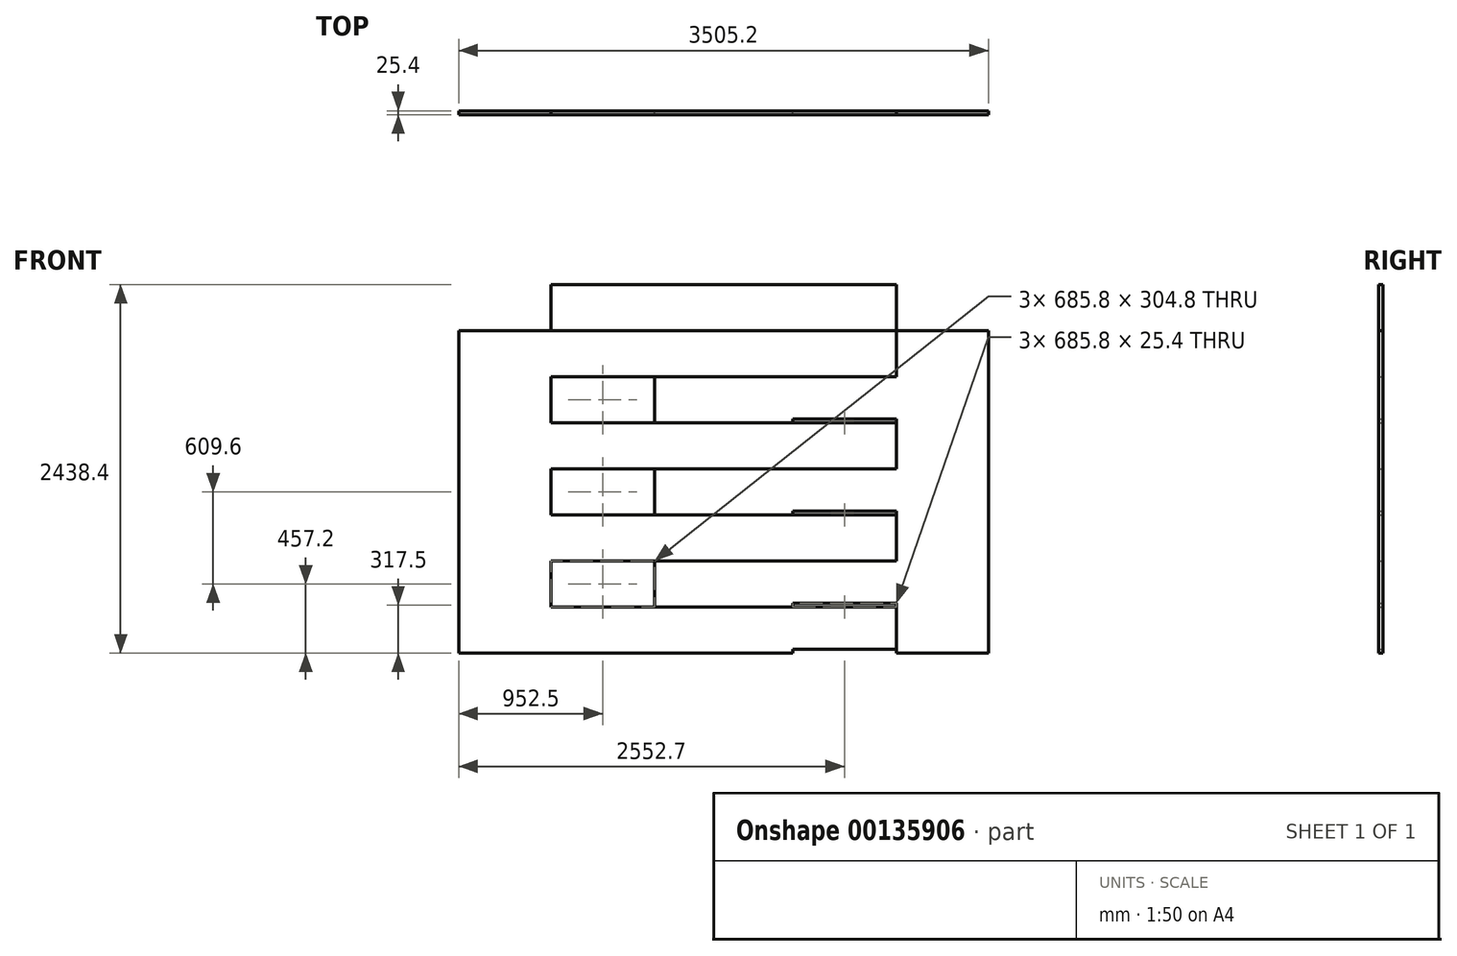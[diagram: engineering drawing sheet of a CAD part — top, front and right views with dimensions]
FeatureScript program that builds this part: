
annotation { "Feature Type Name" : "Feature", "Feature Type Description" : "" }
export const myFeature = defineFeature(function(context is Context, id is Id, definition is map)
    precondition{}
    {
        {
            var Q0;
            Q0=qCreatedBy(makeId("Front.planeOp"),FACE);
            var sketch = newSketch(context, id + "F0", { "sketchPlane" : qUnion([Q0])});
            skLineSegment(sketch, "E0.bottom", {"start": v(1143, 1270) * mm, "end": v(-1143, 1270) * mm});
            skLineSegment(sketch, "E0.top", {"start": v(1143, -1270) * mm, "end": v(-1143, -1270) * mm});
            skLineSegment(sketch, "E0.left", {"start": v(1143, 1270) * mm, "end": v(1143, 558.8) * mm});
            skLineSegment(sketch, "E0.right", {"start": v(-1143, 1270) * mm, "end": v(-1143, 863.6) * mm});
            skPoint(sketch, "E0.middle", {"position": v(0, 0) * mm});
            skLineSegment(sketch, "E1.bottom", {"start": v(-457.2, -1270) * mm, "end": v(457.2, -1270) * mm});
            skLineSegment(sketch, "E1.top", {"start": v(-457.2, 762) * mm, "end": v(457.2, 762) * mm});
            skLineSegment(sketch, "E1.left", {"start": v(-457.2, -1270) * mm, "end": v(-457.2, 762) * mm});
            skLineSegment(sketch, "E1.right", {"start": v(457.2, -1270) * mm, "end": v(457.2, 762) * mm});
            skLineSegment(sketch, "E2.bottom", {"start": v(-1143, 1270) * mm, "end": v(1143, 1270) * mm});
            skLineSegment(sketch, "E2.top", {"start": v(-1143, 1168.4) * mm, "end": v(1143, 1168.4) * mm});
            skLineSegment(sketch, "E2.left", {"start": v(-1143, 1270) * mm, "end": v(-1143, 1168.4) * mm});
            skLineSegment(sketch, "E2.right", {"start": v(1143, 1270) * mm, "end": v(1143, 1168.4) * mm});
            skLineSegment(sketch, "E3.top", {"start": v(-1143, 863.6) * mm, "end": v(1143, 863.6) * mm});
            skLineSegment(sketch, "E3.left", {"start": v(-1143, 1168.4) * mm, "end": v(-1143, 863.6) * mm});
            skLineSegment(sketch, "E3.right", {"start": v(1143, 1168.4) * mm, "end": v(1143, 863.6) * mm});
            skLineSegment(sketch, "E4.0", {"start": v(-1143, 889) * mm, "end": v(1143, 889) * mm});
            skLineSegment(sketch, "E5.0.1.0", {"start": v(-1143, 584.2) * mm, "end": v(1143, 584.2) * mm});
            skLineSegment(sketch, "E5.0.1.1", {"start": v(-1143, 558.8) * mm, "end": v(1143, 558.8) * mm});
            skLineSegment(sketch, "E5.0.2.0", {"start": v(-1143, 279.4) * mm, "end": v(1143, 279.4) * mm});
            skLineSegment(sketch, "E5.0.2.1", {"start": v(-1143, 254) * mm, "end": v(1143, 254) * mm});
            skLineSegment(sketch, "E5.0.3.0", {"start": v(-1143, -25.4) * mm, "end": v(1143, -25.4) * mm});
            skLineSegment(sketch, "E5.0.3.1", {"start": v(-1143, -50.8) * mm, "end": v(1143, -50.8) * mm});
            skLineSegment(sketch, "E5.0.4.0", {"start": v(-1143, -330.2) * mm, "end": v(1143, -330.2) * mm});
            skLineSegment(sketch, "E5.0.4.1", {"start": v(-1143, -355.6) * mm, "end": v(1143, -355.6) * mm});
            skLineSegment(sketch, "E5.0.5.0", {"start": v(-1143, -635) * mm, "end": v(1143, -635) * mm});
            skLineSegment(sketch, "E5.0.5.1", {"start": v(-1143, -660.4) * mm, "end": v(1143, -660.4) * mm});
            skLineSegment(sketch, "E5.0.6.0", {"start": v(-1143, -939.8) * mm, "end": v(1143, -939.8) * mm});
            skLineSegment(sketch, "E5.0.6.1", {"start": v(-1143, -965.2) * mm, "end": v(1143, -965.2) * mm});
            skLineSegment(sketch, "E5.0.7.0", {"start": v(-1143, -1244.6) * mm, "end": v(1143, -1244.6) * mm});
            skLineSegment(sketch, "E5.0.7.1", {"start": v(-1143, -1270) * mm, "end": v(1143, -1270) * mm});
            skLineSegment(sketch, "E5.direction1", {"start": v(-1143, 889) * mm, "end": v(-1117.6, 889) * mm, "construction": true});
            skLineSegment(sketch, "E5.direction2", {"start": v(-1143, 889) * mm, "end": v(-1143, 863.6) * mm, "construction": true});
            skLineSegment(sketch, "E6.bottom", {"start": v(-1143, 863.6) * mm, "end": v(-1752.6, 863.6) * mm});
            skLineSegment(sketch, "E6.top", {"start": v(-1143, -1270) * mm, "end": v(-1752.6, -1270) * mm});
            skLineSegment(sketch, "E6.left", {"start": v(-1143, 584.2) * mm, "end": v(-1143, 254) * mm});
            skLineSegment(sketch, "E6.right", {"start": v(-1752.6, 863.6) * mm, "end": v(-1752.6, -1270) * mm});
            skLineSegment(sketch, "E7.bottom", {"start": v(1143, 863.6) * mm, "end": v(1752.6, 863.6) * mm});
            skLineSegment(sketch, "E7.top", {"start": v(1143, -1270) * mm, "end": v(1752.6, -1270) * mm});
            skLineSegment(sketch, "E7.left", {"start": v(1143, 863.6) * mm, "end": v(1143, 558.8) * mm});
            skLineSegment(sketch, "E7.right", {"start": v(1752.6, 863.6) * mm, "end": v(1752.6, -1270) * mm});
            skLineSegment(sketch, "E8.trimOffspring", {"start": v(-1143, -25.4) * mm, "end": v(-1143, -355.6) * mm});
            skLineSegment(sketch, "E9.trimOffspring", {"start": v(-1143, -635) * mm, "end": v(-1143, -965.2) * mm});
            skLineSegment(sketch, "E10.trimOffspring", {"start": v(-1143, -1244.6) * mm, "end": v(-1143, -1270) * mm});
            skLineSegment(sketch, "E11.trimOffspring", {"start": v(1143, -939.8) * mm, "end": v(1143, -1270) * mm});
            skLineSegment(sketch, "E12.trimOffspring", {"start": v(1143, -330.2) * mm, "end": v(1143, -660.4) * mm});
            skLineSegment(sketch, "E13.trimOffspring", {"start": v(1143, 279.4) * mm, "end": v(1143, -50.8) * mm});
            skSolve(sketch);
        }
        {
            var Q0;
            {var subQ33=sQuery(id+"F0.wireOp",EDGE,"E1.top");Q0=makeQuery(id+"F0.imprint","IMPRINT",FACE,{"disambiguationData":[TD([[makeQuery(id+"F0.imprint","IMPRINT",EDGE,{"derivedFrom":subQ33}),1.0]])]});}
            var Q1;
            {var subQ0=sQuery(id+"F0.wireOp",EDGE,"E1.top");Q1=makeQuery(id+"F0.imprint","IMPRINT",FACE,{"disambiguationData":[TD([[makeQuery(id+"F0.imprint","IMPRINT",EDGE,{"derivedFrom":subQ0}),-1.0]])]});}
            var Q2;
            {var subQ0=sQuery(id+"F0.wireOp",EDGE,"E5.0.3.0");var subQ1=sQuery(id+"F0.wireOp",EDGE,"E1.left");var subQ2=makeQuery(id+"F0.imprint","INTERSECT",VERTEX,{"derivedFrom":[subQ1,subQ0]});Q2=makeQuery(id+"F0.imprint","IMPRINT",FACE,{"disambiguationData":[TD([[makeQuery(id+"F0.imprint","IMPRINT",EDGE,{"disambiguationData":[TD([[subQ2,-1.0]])],"derivedFrom":subQ1}),-1.0]])]});}
            var Q3;
            {var subQ0=sQuery(id+"F0.wireOp",EDGE,"E5.0.3.0");var subQ1=sQuery(id+"F0.wireOp",EDGE,"E1.right");var subQ2=makeQuery(id+"F0.imprint","INTERSECT",VERTEX,{"derivedFrom":[subQ1,subQ0]});Q3=makeQuery(id+"F0.imprint","IMPRINT",FACE,{"disambiguationData":[TD([[makeQuery(id+"F0.imprint","IMPRINT",EDGE,{"disambiguationData":[TD([[subQ2,-1.0]])],"derivedFrom":subQ1}),-1.0]])]});}
            var Q4;
            {var subQ0=sQuery(id+"F0.wireOp",EDGE,"E5.0.5.0");var subQ1=sQuery(id+"F0.wireOp",EDGE,"E1.left");var subQ2=makeQuery(id+"F0.imprint","INTERSECT",VERTEX,{"derivedFrom":[subQ1,subQ0]});Q4=makeQuery(id+"F0.imprint","IMPRINT",FACE,{"disambiguationData":[TD([[makeQuery(id+"F0.imprint","IMPRINT",EDGE,{"disambiguationData":[TD([[subQ2,-1.0]])],"derivedFrom":subQ1}),-1.0]])]});}
            var Q5;
            {var subQ0=sQuery(id+"F0.wireOp",EDGE,"E5.0.5.0");var subQ1=sQuery(id+"F0.wireOp",EDGE,"E1.right");var subQ2=makeQuery(id+"F0.imprint","INTERSECT",VERTEX,{"derivedFrom":[subQ1,subQ0]});Q5=makeQuery(id+"F0.imprint","IMPRINT",FACE,{"disambiguationData":[TD([[makeQuery(id+"F0.imprint","IMPRINT",EDGE,{"disambiguationData":[TD([[subQ2,-1.0]])],"derivedFrom":subQ1}),-1.0]])]});}
            var Q6;
            {var subQ0=sQuery(id+"F0.wireOp",EDGE,"E5.0.7.0");var subQ1=sQuery(id+"F0.wireOp",EDGE,"E1.left");var subQ2=makeQuery(id+"F0.imprint","INTERSECT",VERTEX,{"derivedFrom":[subQ1,subQ0]});Q6=makeQuery(id+"F0.imprint","IMPRINT",FACE,{"disambiguationData":[TD([[makeQuery(id+"F0.imprint","IMPRINT",EDGE,{"disambiguationData":[TD([[subQ2,-1.0]])],"derivedFrom":subQ1}),-1.0]])]});}
            var Q7;
            {var subQ0=sQuery(id+"F0.wireOp",EDGE,"E5.0.7.0");var subQ1=sQuery(id+"F0.wireOp",EDGE,"E1.right");var subQ2=makeQuery(id+"F0.imprint","INTERSECT",VERTEX,{"derivedFrom":[subQ1,subQ0]});Q7=makeQuery(id+"F0.imprint","IMPRINT",FACE,{"disambiguationData":[TD([[makeQuery(id+"F0.imprint","IMPRINT",EDGE,{"disambiguationData":[TD([[subQ2,-1.0]])],"derivedFrom":subQ1}),-1.0]])]});}
            var Q8;
            {var subQ5=sQuery(id+"F0.wireOp",EDGE,"E10.trimOffspring");Q8=makeQuery(id+"F0.imprint","IMPRINT",FACE,{"disambiguationData":[TD([[makeQuery(id+"F0.imprint","IMPRINT",EDGE,{"derivedFrom":subQ5}),1.0]])]});}
            var Q9;
            {var subQ0=sQuery(id+"F0.wireOp",EDGE,"E5.0.7.1");var subQ1=sQuery(id+"F0.wireOp",EDGE,"E1.left");var subQ2=makeQuery(id+"F0.imprint","INTERSECT",VERTEX,{"derivedFrom":[subQ1,subQ0]});Q9=makeQuery(id+"F0.imprint","IMPRINT",FACE,{"disambiguationData":[TD([[makeQuery(id+"F0.imprint","IMPRINT",EDGE,{"disambiguationData":[TD([[subQ2,-1.0]])],"derivedFrom":subQ1}),-1.0]])]});}
            var Q10;
            {var subQ0=sQuery(id+"F0.wireOp",EDGE,"E5.0.7.1");var subQ1=sQuery(id+"F0.wireOp",EDGE,"E1.right");var subQ2=makeQuery(id+"F0.imprint","INTERSECT",VERTEX,{"derivedFrom":[subQ1,subQ0]});Q10=makeQuery(id+"F0.imprint","IMPRINT",FACE,{"disambiguationData":[TD([[makeQuery(id+"F0.imprint","IMPRINT",EDGE,{"disambiguationData":[TD([[subQ2,-1.0]])],"derivedFrom":subQ1}),-1.0]])]});}
            var Q11;
            {var subQ0=sQuery(id+"F0.wireOp",EDGE,"E5.0.5.1");var subQ1=sQuery(id+"F0.wireOp",EDGE,"E1.left");var subQ2=makeQuery(id+"F0.imprint","INTERSECT",VERTEX,{"derivedFrom":[subQ1,subQ0]});Q11=makeQuery(id+"F0.imprint","IMPRINT",FACE,{"disambiguationData":[TD([[makeQuery(id+"F0.imprint","IMPRINT",EDGE,{"disambiguationData":[TD([[subQ2,-1.0]])],"derivedFrom":subQ1}),1.0]])]});}
            var Q12;
            {var subQ0=sQuery(id+"F0.wireOp",EDGE,"E5.0.5.1");var subQ1=sQuery(id+"F0.wireOp",EDGE,"E1.left");var subQ2=makeQuery(id+"F0.imprint","INTERSECT",VERTEX,{"derivedFrom":[subQ1,subQ0]});Q12=makeQuery(id+"F0.imprint","IMPRINT",FACE,{"disambiguationData":[TD([[makeQuery(id+"F0.imprint","IMPRINT",EDGE,{"disambiguationData":[TD([[subQ2,-1.0]])],"derivedFrom":subQ1}),-1.0]])]});}
            var Q13;
            {var subQ0=sQuery(id+"F0.wireOp",EDGE,"E5.0.5.1");var subQ1=sQuery(id+"F0.wireOp",EDGE,"E1.right");var subQ2=makeQuery(id+"F0.imprint","INTERSECT",VERTEX,{"derivedFrom":[subQ1,subQ0]});Q13=makeQuery(id+"F0.imprint","IMPRINT",FACE,{"disambiguationData":[TD([[makeQuery(id+"F0.imprint","IMPRINT",EDGE,{"disambiguationData":[TD([[subQ2,-1.0]])],"derivedFrom":subQ1}),-1.0]])]});}
            var Q14;
            {var subQ0=sQuery(id+"F0.wireOp",EDGE,"E5.0.3.1");var subQ1=sQuery(id+"F0.wireOp",EDGE,"E1.left");var subQ2=makeQuery(id+"F0.imprint","INTERSECT",VERTEX,{"derivedFrom":[subQ1,subQ0]});Q14=makeQuery(id+"F0.imprint","IMPRINT",FACE,{"disambiguationData":[TD([[makeQuery(id+"F0.imprint","IMPRINT",EDGE,{"disambiguationData":[TD([[subQ2,-1.0]])],"derivedFrom":subQ1}),1.0]])]});}
            var Q15;
            {var subQ0=sQuery(id+"F0.wireOp",EDGE,"E5.0.3.1");var subQ1=sQuery(id+"F0.wireOp",EDGE,"E1.left");var subQ2=makeQuery(id+"F0.imprint","INTERSECT",VERTEX,{"derivedFrom":[subQ1,subQ0]});Q15=makeQuery(id+"F0.imprint","IMPRINT",FACE,{"disambiguationData":[TD([[makeQuery(id+"F0.imprint","IMPRINT",EDGE,{"disambiguationData":[TD([[subQ2,-1.0]])],"derivedFrom":subQ1}),-1.0]])]});}
            var Q16;
            {var subQ0=sQuery(id+"F0.wireOp",EDGE,"E5.0.3.1");var subQ1=sQuery(id+"F0.wireOp",EDGE,"E1.right");var subQ2=makeQuery(id+"F0.imprint","INTERSECT",VERTEX,{"derivedFrom":[subQ1,subQ0]});Q16=makeQuery(id+"F0.imprint","IMPRINT",FACE,{"disambiguationData":[TD([[makeQuery(id+"F0.imprint","IMPRINT",EDGE,{"disambiguationData":[TD([[subQ2,-1.0]])],"derivedFrom":subQ1}),-1.0]])]});}
            var Q17;
            {var subQ0=sQuery(id+"F0.wireOp",EDGE,"E5.0.1.1");var subQ1=sQuery(id+"F0.wireOp",EDGE,"E1.left");var subQ2=makeQuery(id+"F0.imprint","INTERSECT",VERTEX,{"derivedFrom":[subQ1,subQ0]});Q17=makeQuery(id+"F0.imprint","IMPRINT",FACE,{"disambiguationData":[TD([[makeQuery(id+"F0.imprint","IMPRINT",EDGE,{"disambiguationData":[TD([[subQ2,-1.0]])],"derivedFrom":subQ1}),1.0]])]});}
            var Q18;
            {var subQ0=sQuery(id+"F0.wireOp",EDGE,"E5.0.1.1");var subQ1=sQuery(id+"F0.wireOp",EDGE,"E1.left");var subQ2=makeQuery(id+"F0.imprint","INTERSECT",VERTEX,{"derivedFrom":[subQ1,subQ0]});Q18=makeQuery(id+"F0.imprint","IMPRINT",FACE,{"disambiguationData":[TD([[makeQuery(id+"F0.imprint","IMPRINT",EDGE,{"disambiguationData":[TD([[subQ2,-1.0]])],"derivedFrom":subQ1}),-1.0]])]});}
            var Q19;
            {var subQ0=sQuery(id+"F0.wireOp",EDGE,"E5.0.1.1");var subQ1=sQuery(id+"F0.wireOp",EDGE,"E1.right");var subQ2=makeQuery(id+"F0.imprint","INTERSECT",VERTEX,{"derivedFrom":[subQ1,subQ0]});Q19=makeQuery(id+"F0.imprint","IMPRINT",FACE,{"disambiguationData":[TD([[makeQuery(id+"F0.imprint","IMPRINT",EDGE,{"disambiguationData":[TD([[subQ2,-1.0]])],"derivedFrom":subQ1}),-1.0]])]});}
            extrude(context, id + "F1", {"entities" : qUnion([Q0, Q1, Q2, Q3, Q4, Q5, Q6, Q7, Q8, Q9, Q10, Q11, Q12, Q13, Q14, Q15, Q16, Q17, Q18, Q19]), "depth" : 25.4 * mm});
        }
        {
            var Q0;
            {var subQ20=sQuery(id+"F0.wireOp",EDGE,"E7.bottom");Q0=makeQuery(id+"F0.imprint","IMPRINT",FACE,{"disambiguationData":[TD([[makeQuery(id+"F0.imprint","IMPRINT",EDGE,{"derivedFrom":subQ20}),-1.0]])]});}
            var Q1;
            {var subQ0=sQuery(id+"F0.wireOp",EDGE,"E5.0.2.0");var subQ1=sQuery(id+"F0.wireOp",EDGE,"E1.left");var subQ2=makeQuery(id+"F0.imprint","INTERSECT",VERTEX,{"derivedFrom":[subQ1,subQ0]});Q1=makeQuery(id+"F0.imprint","IMPRINT",FACE,{"disambiguationData":[TD([[makeQuery(id+"F0.imprint","IMPRINT",EDGE,{"disambiguationData":[TD([[subQ2,-1.0]])],"derivedFrom":subQ1}),-1.0]])]});}
            var Q2;
            {var subQ0=sQuery(id+"F0.wireOp",EDGE,"E5.0.2.0");var subQ1=sQuery(id+"F0.wireOp",EDGE,"E1.left");var subQ2=makeQuery(id+"F0.imprint","INTERSECT",VERTEX,{"derivedFrom":[subQ1,subQ0]});Q2=makeQuery(id+"F0.imprint","IMPRINT",FACE,{"disambiguationData":[TD([[makeQuery(id+"F0.imprint","IMPRINT",EDGE,{"disambiguationData":[TD([[subQ2,-1.0]])],"derivedFrom":subQ1}),1.0]])]});}
            var Q3;
            {var subQ0=sQuery(id+"F0.wireOp",EDGE,"E5.0.4.0");var subQ1=sQuery(id+"F0.wireOp",EDGE,"E1.left");var subQ2=makeQuery(id+"F0.imprint","INTERSECT",VERTEX,{"derivedFrom":[subQ1,subQ0]});Q3=makeQuery(id+"F0.imprint","IMPRINT",FACE,{"disambiguationData":[TD([[makeQuery(id+"F0.imprint","IMPRINT",EDGE,{"disambiguationData":[TD([[subQ2,-1.0]])],"derivedFrom":subQ1}),1.0]])]});}
            var Q4;
            {var subQ0=sQuery(id+"F0.wireOp",EDGE,"E5.0.4.0");var subQ1=sQuery(id+"F0.wireOp",EDGE,"E1.left");var subQ2=makeQuery(id+"F0.imprint","INTERSECT",VERTEX,{"derivedFrom":[subQ1,subQ0]});Q4=makeQuery(id+"F0.imprint","IMPRINT",FACE,{"disambiguationData":[TD([[makeQuery(id+"F0.imprint","IMPRINT",EDGE,{"disambiguationData":[TD([[subQ2,-1.0]])],"derivedFrom":subQ1}),-1.0]])]});}
            var Q5;
            {var subQ0=sQuery(id+"F0.wireOp",EDGE,"E5.0.6.0");var subQ1=sQuery(id+"F0.wireOp",EDGE,"E1.left");var subQ2=makeQuery(id+"F0.imprint","INTERSECT",VERTEX,{"derivedFrom":[subQ1,subQ0]});Q5=makeQuery(id+"F0.imprint","IMPRINT",FACE,{"disambiguationData":[TD([[makeQuery(id+"F0.imprint","IMPRINT",EDGE,{"disambiguationData":[TD([[subQ2,-1.0]])],"derivedFrom":subQ1}),1.0]])]});}
            var Q6;
            {var subQ0=sQuery(id+"F0.wireOp",EDGE,"E5.0.6.0");var subQ1=sQuery(id+"F0.wireOp",EDGE,"E1.left");var subQ2=makeQuery(id+"F0.imprint","INTERSECT",VERTEX,{"derivedFrom":[subQ1,subQ0]});Q6=makeQuery(id+"F0.imprint","IMPRINT",FACE,{"disambiguationData":[TD([[makeQuery(id+"F0.imprint","IMPRINT",EDGE,{"disambiguationData":[TD([[subQ2,-1.0]])],"derivedFrom":subQ1}),-1.0]])]});}
            var Q7;
            {var subQ0=sQuery(id+"F0.wireOp",EDGE,"E5.0.2.1");var subQ1=sQuery(id+"F0.wireOp",EDGE,"E1.left");var subQ2=makeQuery(id+"F0.imprint","INTERSECT",VERTEX,{"derivedFrom":[subQ1,subQ0]});Q7=makeQuery(id+"F0.imprint","IMPRINT",FACE,{"disambiguationData":[TD([[makeQuery(id+"F0.imprint","IMPRINT",EDGE,{"disambiguationData":[TD([[subQ2,-1.0]])],"derivedFrom":subQ1}),1.0]])]});}
            var Q8;
            {var subQ0=sQuery(id+"F0.wireOp",EDGE,"E5.0.2.1");var subQ1=sQuery(id+"F0.wireOp",EDGE,"E1.left");var subQ2=makeQuery(id+"F0.imprint","INTERSECT",VERTEX,{"derivedFrom":[subQ1,subQ0]});Q8=makeQuery(id+"F0.imprint","IMPRINT",FACE,{"disambiguationData":[TD([[makeQuery(id+"F0.imprint","IMPRINT",EDGE,{"disambiguationData":[TD([[subQ2,-1.0]])],"derivedFrom":subQ1}),-1.0]])]});}
            var Q9;
            {var subQ0=sQuery(id+"F0.wireOp",EDGE,"E5.0.2.1");var subQ1=sQuery(id+"F0.wireOp",EDGE,"E1.right");var subQ2=makeQuery(id+"F0.imprint","INTERSECT",VERTEX,{"derivedFrom":[subQ1,subQ0]});Q9=makeQuery(id+"F0.imprint","IMPRINT",FACE,{"disambiguationData":[TD([[makeQuery(id+"F0.imprint","IMPRINT",EDGE,{"disambiguationData":[TD([[subQ2,-1.0]])],"derivedFrom":subQ1}),-1.0]])]});}
            var Q10;
            {var subQ0=sQuery(id+"F0.wireOp",EDGE,"E5.0.4.1");var subQ1=sQuery(id+"F0.wireOp",EDGE,"E1.left");var subQ2=makeQuery(id+"F0.imprint","INTERSECT",VERTEX,{"derivedFrom":[subQ1,subQ0]});Q10=makeQuery(id+"F0.imprint","IMPRINT",FACE,{"disambiguationData":[TD([[makeQuery(id+"F0.imprint","IMPRINT",EDGE,{"disambiguationData":[TD([[subQ2,-1.0]])],"derivedFrom":subQ1}),1.0]])]});}
            var Q11;
            {var subQ0=sQuery(id+"F0.wireOp",EDGE,"E5.0.4.1");var subQ1=sQuery(id+"F0.wireOp",EDGE,"E1.left");var subQ2=makeQuery(id+"F0.imprint","INTERSECT",VERTEX,{"derivedFrom":[subQ1,subQ0]});Q11=makeQuery(id+"F0.imprint","IMPRINT",FACE,{"disambiguationData":[TD([[makeQuery(id+"F0.imprint","IMPRINT",EDGE,{"disambiguationData":[TD([[subQ2,-1.0]])],"derivedFrom":subQ1}),-1.0]])]});}
            var Q12;
            {var subQ0=sQuery(id+"F0.wireOp",EDGE,"E5.0.4.1");var subQ1=sQuery(id+"F0.wireOp",EDGE,"E1.right");var subQ2=makeQuery(id+"F0.imprint","INTERSECT",VERTEX,{"derivedFrom":[subQ1,subQ0]});Q12=makeQuery(id+"F0.imprint","IMPRINT",FACE,{"disambiguationData":[TD([[makeQuery(id+"F0.imprint","IMPRINT",EDGE,{"disambiguationData":[TD([[subQ2,-1.0]])],"derivedFrom":subQ1}),-1.0]])]});}
            var Q13;
            {var subQ0=sQuery(id+"F0.wireOp",EDGE,"E5.0.6.1");var subQ1=sQuery(id+"F0.wireOp",EDGE,"E1.left");var subQ2=makeQuery(id+"F0.imprint","INTERSECT",VERTEX,{"derivedFrom":[subQ1,subQ0]});Q13=makeQuery(id+"F0.imprint","IMPRINT",FACE,{"disambiguationData":[TD([[makeQuery(id+"F0.imprint","IMPRINT",EDGE,{"disambiguationData":[TD([[subQ2,-1.0]])],"derivedFrom":subQ1}),1.0]])]});}
            var Q14;
            {var subQ0=sQuery(id+"F0.wireOp",EDGE,"E5.0.6.1");var subQ1=sQuery(id+"F0.wireOp",EDGE,"E1.left");var subQ2=makeQuery(id+"F0.imprint","INTERSECT",VERTEX,{"derivedFrom":[subQ1,subQ0]});Q14=makeQuery(id+"F0.imprint","IMPRINT",FACE,{"disambiguationData":[TD([[makeQuery(id+"F0.imprint","IMPRINT",EDGE,{"disambiguationData":[TD([[subQ2,-1.0]])],"derivedFrom":subQ1}),-1.0]])]});}
            var Q15;
            {var subQ0=sQuery(id+"F0.wireOp",EDGE,"E5.0.6.1");var subQ1=sQuery(id+"F0.wireOp",EDGE,"E1.right");var subQ2=makeQuery(id+"F0.imprint","INTERSECT",VERTEX,{"derivedFrom":[subQ1,subQ0]});Q15=makeQuery(id+"F0.imprint","IMPRINT",FACE,{"disambiguationData":[TD([[makeQuery(id+"F0.imprint","IMPRINT",EDGE,{"disambiguationData":[TD([[subQ2,-1.0]])],"derivedFrom":subQ1}),-1.0]])]});}
            extrude(context, id + "F2", {"entities" : qUnion([Q0, Q1, Q2, Q3, Q4, Q5, Q6, Q7, Q8, Q9, Q10, Q11, Q12, Q13, Q14, Q15]), "depth" : 25.4 * mm});
        }
        {
            var Q0;
            {var subQ0=sQuery(id+"F0.wireOp",EDGE,"E2.top");Q0=makeQuery(id+"F0.imprint","IMPRINT",FACE,{"disambiguationData":[TD([[makeQuery(id+"F0.imprint","IMPRINT",EDGE,{"derivedFrom":subQ0}),-1.0]])]});}
            var Q1;
            Q1=makeQuery(id+"F0.imprint","IMPRINT",FACE,{"disambiguationData":[TD([[makeQuery(id+"F0.imprint","IMPRINT",EDGE,{"derivedFrom":sQuery(id+"F0.wireOp",EDGE,"E2.bottom")}),-1.0]])]});
            var Q2;
            {var subQ0=sQuery(id+"F0.wireOp",EDGE,"E3.top");Q2=makeQuery(id+"F0.imprint","IMPRINT",FACE,{"disambiguationData":[TD([[makeQuery(id+"F0.imprint","IMPRINT",EDGE,{"derivedFrom":subQ0}),1.0]])]});}
            extrude(context, id + "F3", {"entities" : qUnion([Q0, Q1, Q2]), "depth" : 25.4 * mm});
        }
    });
